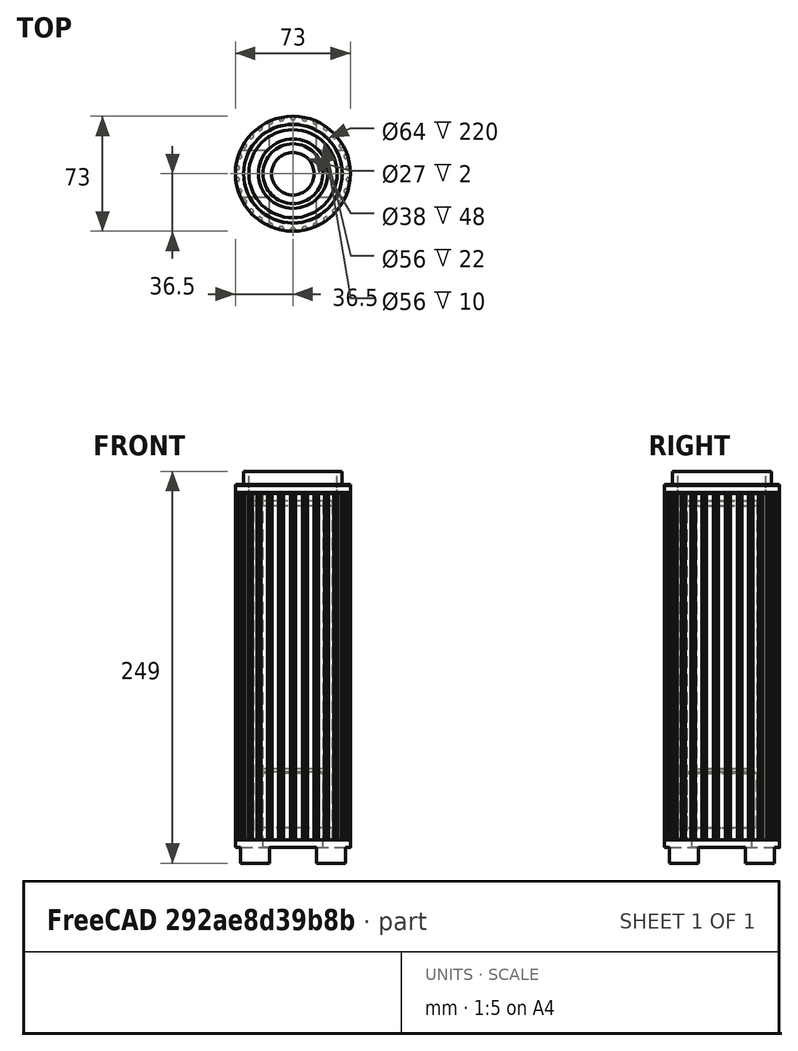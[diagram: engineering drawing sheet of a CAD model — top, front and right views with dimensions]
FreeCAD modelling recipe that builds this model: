
FCSTD DOCUMENT  (FreeCAD 0.15R4671 (Git))
Label: pica-small-v6
License: All rights reserved
LicenseURL: http://en.wikipedia.org/wiki/All_rights_reserved
objects: Drawing::FeatureView×16, Part::Cylinder×14, Part::Cut×7, Drawing::FeatureViewPart×7, Part::MultiFuse×6, Drawing::FeaturePage×2, Part::Box×2, Part::Part2DObjectPython×1, PartDesign::Pad×1, Part::Chamfer×1
note: 33 computed .brp shape members not serialized (recipe doc carries the construction recipe); baked Part::Feature solids carry a one-line shape summary decoded from their .brp

FEATURE [Part::Part2DObjectPython] InvoluteGear  # Draft 2D object (typed FeaturePython)
  ExternalGear = true
  HighPrecision = true
  Modules = 2.5
  NumberOfTeeth = 30
  PressureAngle = 20
FEATURE [PartDesign::Pad] Pad
  Length = 220
  Length2 = 100
  Sketch = -> InvoluteGear
  Type = 0
FEATURE [Part::Cylinder] Cylinder
  Angle = 360
  Height = 240
  Placement = pos=(0,0,-10) rot=(0,0,1;0rad)
  Radius = 32
FEATURE [Part::Cut] Cut  label="Final"
  Base = -> Pad
  Tool = -> Cylinder
FEATURE [Part::Cylinder] Cylinder001
  Angle = 360
  Height = 400
  Radius = 36.5
FEATURE [Part::Cylinder] Cylinder002
  Angle = 360
  Height = 400
  Radius = 100
FEATURE [Part::Cut] Cut001
  Base = -> Cylinder002
  Tool = -> Cylinder001
FEATURE [Part::Cut] Cut002  label="Shade"
  Base = -> Cut
  Placement = pos=(0,0,15) rot=(0,0,1;0rad)
  Tool = -> Cut001
FEATURE [Part::Cylinder] Cylinder003
  Angle = 360
  Height = 15
  Radius = 36.5
FEATURE [Part::Cylinder] Cylinder004
  Angle = 360
  Height = 22.5
  Radius = 31.3
FEATURE [Part::MultiFuse] Fusion  label="Base Fusion"
  Shapes = -> [Cylinder004,Cylinder003]
FEATURE [Drawing::FeatureViewPart] FrontView  label="Shade Side"
  Direction = (0,-1,0)
  HiddenWidth = 0.15
  LineWidth = 0.35
  Rotation = 90
  ShowHiddenLines = true
  ShowSmoothLines = false
  Source = -> Cut002
  Tolerance = 0.05
  ViewResult = <blob: 104580 chars omitted>
  Visible = true
  X = 80
  Y = 270
FEATURE [Drawing::FeatureViewPart] View001  label="Shade Top"
  Direction = (0,0,1)
  HiddenWidth = 0.15
  LineWidth = 0.35
  Rotation = 0
  ShowHiddenLines = false
  ShowSmoothLines = false
  Source = -> Cut002
  Tolerance = 0.05
  ViewResult = <blob: 17331 chars omitted>
  Visible = true
  X = 300
  Y = 80
FEATURE [Drawing::FeatureView] dim006  label="Base Radius"
  Rotation = 0
  ViewResult = <g   >\n <circle cx ="300.000000" cy ="170.000000" r="0.500000" stroke="none" fill="rgb(0,0,0)" /> \n<line x1="255.718312" y1="135.631286" x2="300.000000" y2="170.000000" style="stroke:rgb(0,0,0);stroke-width:0.30" />\n<polygon points="275.273643,150.808927 277.030448,153.438307 278.433561,153.261461 278.256715,151.858348" style="fill:rgb(0,0,0);stroke:rgb(0,0,0);stroke-width:0" />\n<line x1="255.718312" y1="135.631286" x2="231.639949" y2="135.631286" style="stroke:rgb(0,0,0);stroke-width:0.30" />\n<text x="219.448373" y="136.850443" font-family="Arial" font-size="3.6" fill="rgb(0,0,0)" text-anchor="inherit"  >R31.3</text>\n<!--31.3-->\n<!--R%3.3f-->\n</g> 
  Visible = true
  X = 0
  Y = 0
FEATURE [Drawing::FeatureView] centerLines
  Rotation = 0
  ViewResult = <g  transform="scale(1.000000,1.000000)" stroke="rgb(0,0,0)"  stroke-width="0.300000" >\n<path d="M 300.000000,170.000000 L 300.000000,168.000000 M 300.000000,166.000000 L 300.000000,160.000000 M 300.000000,158.000000 L 300.000000,156.000000 "/>\n<path d="M 300.000000,170.000000 L 302.000000,170.000000 M 304.000000,170.000000 L 310.000000,170.000000 M 312.000000,170.000000 L 314.000000,170.000000 "/>\n<path d="M 300.000000,170.000000 L 300.000000,172.000000 M 300.000000,174.000000 L 300.000000,180.000000 M 300.000000,182.000000 L 300.000000,184.000000 "/>\n<path d="M 300.000000,170.000000 L 298.000000,170.000000 M 296.000000,170.000000 L 290.000000,170.000000 M 288.000000,170.000000 L 286.000000,170.000000 "/>\n</g> 
  Visible = true
  X = 0
  Y = 0
FEATURE [Drawing::FeatureView] centerLines001
  Rotation = 0
  ViewResult = <g  transform="scale(1.000000,1.000000)" stroke="rgb(0,0,0)"  stroke-width="0.300000" >\n<path d="M 300.000000,80.000000 L 300.000000,82.000000 M 300.000000,84.000000 L 300.000000,90.000000 M 300.000000,92.000000 L 300.000000,94.000000 "/>\n<path d="M 300.000000,80.000000 L 302.000000,80.000000 M 304.000000,80.000000 L 310.000000,80.000000 M 312.000000,80.000000 L 314.000000,80.000000 "/>\n<path d="M 300.000000,80.000000 L 300.000000,78.000000 M 300.000000,76.000000 L 300.000000,70.000000 M 300.000000,68.000000 L 300.000000,66.000000 "/>\n<path d="M 300.000000,80.000000 L 298.000000,80.000000 M 296.000000,80.000000 L 290.000000,80.000000 M 288.000000,80.000000 L 286.000000,80.000000 "/>\n</g> 
  Visible = true
  X = 0
  Y = 0
FEATURE [Drawing::FeatureView] dim007  label="Shade Radius"
  Rotation = 0
  ViewResult = <g   >\n <circle cx ="300.000000" cy ="80.000000" r="0.500000" stroke="none" fill="rgb(0,0,0)" /> \n<line x1="340.917441" y1="111.884102" x2="300.000000" y2="80.000000" style="stroke:rgb(0,0,0);stroke-width:0.30" />\n<polygon points="325.241495,99.668933 323.489759,97.036174 322.086308,97.210316 322.260451,98.613767" style="fill:rgb(0,0,0);stroke:rgb(0,0,0);stroke-width:0" />\n<line x1="340.917441" y1="111.884102" x2="365.557939" y2="111.884102" style="stroke:rgb(0,0,0);stroke-width:0.30" />\n<text x="369.473360" y="112.835313" font-family="Arial" font-size="3.6" fill="rgb(0,0,0)" text-anchor="inherit"  >R32</text>\n<!--32.0-->\n<!--R%3.3f-->\n</g> 
  Visible = true
  X = 0
  Y = 0
FEATURE [Part::Cylinder] Cylinder005
  Angle = 360
  Height = 90
  Radius = 13.5
FEATURE [Part::Cylinder] Cylinder006
  Angle = 360
  Height = 58
  Radius = 19
FEATURE [Part::MultiFuse] Fusion002  label="Fixture Mount"
  Shapes = -> [Cylinder005,Cylinder006]
FEATURE [Drawing::FeatureViewPart] View004  label="Base Top"
  Direction = (0,0,1)
  HiddenWidth = 0.15
  LineWidth = 0.35
  Rotation = 0
  ShowHiddenLines = false
  ShowSmoothLines = false
  Tolerance = 0.05
  ViewResult = <g id="Base Top"\n   transform="rotate(0,300,170) translate(300,170) scale(1,1)"\n  >\n<g   stroke="rgb(0, 0, 0)"\n   stroke-width="0.35"\n   stroke-linecap="butt"\n   stroke-linejoin="miter"\n   fill="none"\n   transform="scale(1,-1)"\n  >\n<circle cx ="0" cy ="0" r ="23.3" /><circle cx ="0" cy ="0" r ="15" /><circle cx ="0" cy ="0" r ="31.3" /><circle cx ="0" cy ="0" r ="36.5" /></g>\n</g>
  Visible = true
  X = 300
  Y = 170
FEATURE [Drawing::FeatureViewPart] View005  label="Base Side"
  Direction = (0,-1,0)
  HiddenWidth = 0.15
  LineWidth = 0.35
  Rotation = 90
  ShowHiddenLines = false
  ShowSmoothLines = false
  Tolerance = 0.05
  ViewResult = <blob: 2600 chars omitted>
  Visible = true
  X = 80
  Y = 270
FEATURE [Drawing::FeatureViewPart] View  label="Base Side001"
  Direction = (0,-1,0)
  HiddenWidth = 0.15
  LineWidth = 0.35
  Rotation = 90
  ShowHiddenLines = false
  ShowSmoothLines = false
  Tolerance = 0.05
  ViewResult = <blob: 2605 chars omitted>
  Visible = true
  X = 180
  Y = 100
FEATURE [Drawing::FeatureViewPart] View006  label="Base Top001"
  Direction = (0,0,-1)
  HiddenWidth = 0.15
  LineWidth = 0.35
  Rotation = 0
  ShowHiddenLines = false
  ShowSmoothLines = false
  Tolerance = 0.05
  ViewResult = <blob: 2659 chars omitted>
  Visible = true
  X = 180
  Y = 170
FEATURE [Drawing::FeatureView] dim010  label="dim001"
  Rotation = 0
  ViewResult = <g   >\n<line x1="158.500000" y1="235.000000" x2="177.679727" y2="235.000000" style="stroke:rgb(0,0,0);stroke-width:0.30" />\n<line x1="158.483300" y1="250.000000" x2="177.679727" y2="250.000000" style="stroke:rgb(0,0,0);stroke-width:0.30" />\n<line x1="176.679727" y1="235.000000" x2="176.679727" y2="250.000000" style="stroke:rgb(0,0,0);stroke-width:0.30" />\n<polygon points="176.679727,235.000000 175.679727,238.000000 176.679727,239.000000 177.679727,238.000000" style="fill:rgb(0,0,0);stroke:rgb(0,0,0);stroke-width:0" /><polygon points="176.679727,250.000000 177.679727,247.000000 176.679727,246.000000 175.679727,247.000000" style="fill:rgb(0,0,0);stroke:rgb(0,0,0);stroke-width:0" />\n<text x="183.587709" y="244.783611" font-family="Arial" font-size="3.6" fill="rgb(0,0,0)" text-anchor="inherit" transform="rotate(-90.000000 183.587709,244.783611)" >15</text>\n</g> 
  Visible = true
  X = 0
  Y = 0
FEATURE [Drawing::FeatureView] dim011  label="dim002"
  Rotation = 0
  ViewResult = <g   >\n<line x1="153.300000" y1="228.000000" x2="177.810311" y2="228.000000" style="stroke:rgb(0,0,0);stroke-width:0.30" />\n<line x1="158.500000" y1="235.000000" x2="177.810311" y2="235.000000" style="stroke:rgb(0,0,0);stroke-width:0.30" />\n<line x1="176.810311" y1="228.000000" x2="176.810311" y2="235.000000" style="stroke:rgb(0,0,0);stroke-width:0.30" />\n<polygon points="176.810311,228.000000 177.810311,225.000000 176.810311,224.000000 175.810311,225.000000" style="fill:rgb(0,0,0);stroke:rgb(0,0,0);stroke-width:0" /><polygon points="176.810311,235.000000 175.810311,238.000000 176.810311,239.000000 177.810311,238.000000" style="fill:rgb(0,0,0);stroke:rgb(0,0,0);stroke-width:0" />\n<text x="183.208911" y="232.569545" font-family="Arial" font-size="3.6" fill="rgb(0,0,0)" text-anchor="inherit" transform="rotate(-90.000000 183.208911,232.569545)" >7</text>\n</g> 
  Visible = true
  X = 0
  Y = 0
FEATURE [Drawing::FeatureView] centerLines004
  Rotation = 0
  ViewResult = <g  transform="scale(1.000000,1.000000)" stroke="rgb(0,0,0)"  stroke-width="0.300000" >\n<path d="M 180.000000,169.999925 L 180.000000,167.999925 M 180.000000,165.999925 L 180.000000,159.999925 M 180.000000,157.999925 L 180.000000,155.999925 "/>\n<path d="M 180.000000,169.999925 L 182.000000,169.999925 M 184.000000,169.999925 L 190.000000,169.999925 M 192.000000,169.999925 L 194.000000,169.999925 "/>\n<path d="M 180.000000,169.999925 L 180.000000,171.999925 M 180.000000,173.999925 L 180.000000,179.999925 M 180.000000,181.999925 L 180.000000,183.999925 M 180.000000,185.999925 L 180.000000,186.160469 "/>\n<path d="M 180.000000,169.999925 L 178.000000,169.999925 M 176.000000,169.999925 L 170.000000,169.999925 M 168.000000,169.999925 L 166.583365,169.999925 "/>\n</g> 
  Visible = true
  X = 0
  Y = 0
FEATURE [Drawing::FeatureView] dim
  Rotation = 0
  ViewResult = <g   >\n<line x1="41.500000" y1="25.000000" x2="33.944194" y2="25.000000" style="stroke:rgb(0,0,0);stroke-width:0.30" />\n<line x1="41.500000" y1="245.000000" x2="33.944194" y2="245.000000" style="stroke:rgb(0,0,0);stroke-width:0.30" />\n<line x1="34.944194" y1="25.000000" x2="34.944194" y2="245.000000" style="stroke:rgb(0,0,0);stroke-width:0.30" />\n<polygon points="34.944194,25.000000 33.944194,28.000000 34.944194,29.000000 35.944194,28.000000" style="fill:rgb(0,0,0);stroke:rgb(0,0,0);stroke-width:0" /><polygon points="34.944194,245.000000 35.944194,242.000000 34.944194,241.000000 33.944194,242.000000" style="fill:rgb(0,0,0);stroke:rgb(0,0,0);stroke-width:0" />\n<text x="31.608126" y="136.256650" font-family="Arial" font-size="3.6" fill="rgb(0,0,0)" text-anchor="inherit" transform="rotate(-90.000000 31.608126,136.256650)" >220</text>\n</g> 
  Visible = true
  X = 0
  Y = 0
FEATURE [Drawing::FeatureView] dim012
  Rotation = 0
  ViewResult = <g   >\n<line x1="118.122400" y1="245.000000" x2="126.861722" y2="245.000000" style="stroke:rgb(0,0,0);stroke-width:0.30" />\n<line x1="115.275400" y1="270.000000" x2="126.861722" y2="270.000000" style="stroke:rgb(0,0,0);stroke-width:0.30" />\n<line x1="125.861722" y1="245.000000" x2="125.861722" y2="270.000000" style="stroke:rgb(0,0,0);stroke-width:0.30" />\n<polygon points="125.861722,245.000000 124.861722,248.000000 125.861722,249.000000 126.861722,248.000000" style="fill:rgb(0,0,0);stroke:rgb(0,0,0);stroke-width:0" /><polygon points="125.861722,270.000000 126.861722,267.000000 125.861722,266.000000 124.861722,267.000000" style="fill:rgb(0,0,0);stroke:rgb(0,0,0);stroke-width:0" />\n<text x="132.056471" y="260.197520" font-family="Arial" font-size="3.6" fill="rgb(0,0,0)" text-anchor="inherit" transform="rotate(-90.000000 132.056471,260.197520)" >25</text>\n</g> 
  Visible = true
  X = 0
  Y = 0
FEATURE [Drawing::FeatureView] dim013
  Rotation = 0
  ViewResult = <g   >\n<line x1="143.500000" y1="73.000000" x2="143.500000" y2="45.465562" style="stroke:rgb(0,0,0);stroke-width:0.30" />\n<line x1="216.500000" y1="73.000000" x2="216.500000" y2="45.465562" style="stroke:rgb(0,0,0);stroke-width:0.30" />\n<line x1="143.500000" y1="46.465562" x2="216.500000" y2="46.465562" style="stroke:rgb(0,0,0);stroke-width:0.30" />\n<polygon points="143.500000,46.465562 146.500000,47.465562 147.500000,46.465562 146.500000,45.465562" style="fill:rgb(0,0,0);stroke:rgb(0,0,0);stroke-width:0" /><polygon points="216.500000,46.465562 213.500000,45.465562 212.500000,46.465562 213.500000,47.465562" style="fill:rgb(0,0,0);stroke:rgb(0,0,0);stroke-width:0" />\n<text x="177.413963" y="43.541156" font-family="Arial" font-size="3.6" fill="rgb(0,0,0)" text-anchor="inherit" transform="rotate(0.000000 177.413963,43.541156)" >73</text>\n</g> 
  Visible = true
  X = 0
  Y = 0
FEATURE [Drawing::FeaturePage] AutoDrawing  label="Initial Sketch"
  EditableTexts = FLOYD DIEBEL | 8/22/2015 | 1:1 | 1 | 1 | PICA (SMALL V2) | LAMP WITH SHADE
  Group = -> [FrontView,View001,dim006,centerLines,centerLines001,dim007,View004,View005,dim010,dim011,View,View006,centerLines004,dim,dim012,dim013]
  Template = C:/Program Files/FreeCAD 0.15/data/Mod/Drawing/Templates/A3_Landscape.svg
FEATURE [Part::Cylinder] Cylinder007
  Angle = 360
  Height = 60
  Radius = 22
FEATURE [Part::MultiFuse] Fusion003
  Shapes = -> [Fusion,Cylinder007]
FEATURE [Part::Cut] Cut005  label="Raw"
  Base = -> Fusion003
  Tool = -> Fusion002
FEATURE [Part::Box] Box002  label="Cube002"
  Height = 10
  Length = 100
  Placement = pos=(-50,-15,0) rot=(0,0,1;0rad)
  Width = 30
FEATURE [Part::Box] Box003  label="Cube003"
  Height = 10
  Length = 100
  Placement = pos=(15,-50,0) rot=(0,0,1;1.5708rad)
  Width = 30
FEATURE [Part::MultiFuse] Fusion004  label="Feet Cutout Fusion001"
  Shapes = -> [Box003,Box002]
FEATURE [Part::Cut] Cut006  label="Pre-chamfer"
  Base = -> Cut005
  Tool = -> Fusion004
FEATURE [Part::Chamfer] Chamfer  label="Base"
  Base = -> Cut006
  Edges = 1 edges r=3: [Edge1]
FEATURE [Part::Cylinder] Cylinder008
  Angle = 360
  Height = 5
  Placement = pos=(0,0,8.5) rot=(0,0,1;0rad)
  Radius = 36.5
FEATURE [Part::Cylinder] Cylinder009
  Angle = 360
  Height = 22
  Radius = 31.3
FEATURE [Part::MultiFuse] Fusion005  label="No Cutout"
  Shapes = -> [Cylinder009,Cylinder008]
FEATURE [Part::Cylinder] Cylinder010
  Angle = 360
  Height = 55
  Placement = pos=(0,0,-10) rot=(0,0,1;0rad)
  Radius = 28
FEATURE [Part::Cut] Cut007  label="Joint"
  Base = -> Fusion005
  Placement = pos=(0,0,227) rot=(0,0,1;0rad)
  Tool = -> Cylinder010
FEATURE [Part::Cylinder] Cylinder011
  Angle = 360
  Height = 5
  Placement = pos=(0,0,5) rot=(0,0,1;0rad)
  Radius = 36.5
FEATURE [Part::Cylinder] Cylinder012
  Angle = 360
  Height = 10
  Radius = 31.3
FEATURE [Part::MultiFuse] Fusion006  label="No Cutout001"
  Shapes = -> [Cylinder012,Cylinder011]
FEATURE [Part::Cylinder] Cylinder013
  Angle = 360
  Height = 55
  Placement = pos=(0,0,-10) rot=(0,0,1;0rad)
  Radius = 28
FEATURE [Part::Cut] Cut008  label="Cap"
  Base = -> Fusion006
  Placement = pos=(0,0,230) rot=(0,0,1;0rad)
  Tool = -> Cylinder013
FEATURE [Drawing::FeatureViewPart] View008
  Direction = (1,0,0)
  HiddenWidth = 0.15
  LineWidth = 0.35
  Rotation = 270
  ShowHiddenLines = true
  ShowSmoothLines = false
  Source = -> Chamfer
  Tolerance = 0.05
  ViewResult = <blob: 14622 chars omitted>
  Visible = true
  X = 110
  Y = 150
FEATURE [Drawing::FeatureView] dim001  label="dim014"
  Rotation = 0
  ViewResult = <g> \n  <line x1="89.119500" y1="92.000000" x2="60.460732" y2="92.000000" style="stroke:rgb(0,0,0);stroke-width:0.30" />\n<line x1="89.119500" y1="90.000000" x2="60.460732" y2="90.000000" style="stroke:rgb(0,0,0);stroke-width:0.30" />\n<line x1="61.460732" y1="92.000000" x2="61.460732" y2="90.000000" style="stroke:rgb(0,0,0);stroke-width:0.30" /> \n  <polygon points="61.460732,90.000000 62.460732,87.000000 61.460732,86.000000 60.460732,87.000000" style="fill:rgb(0,0,0);stroke:rgb(0,0,0);stroke-width:0" /><polygon points="61.460732,92.000000 60.460732,95.000000 61.460732,96.000000 62.460732,95.000000" style="fill:rgb(0,0,0);stroke:rgb(0,0,0);stroke-width:0" /> \n  <text x="59.460732" y="91.000000" font-family="arial" font-size="3.6" fill="rgb(0,0,0)" text-anchor="middle" transform="rotate(-90.000000 59.460732,91.000000)" >2</text> </g>
  Visible = true
  X = 0
  Y = 0
FEATURE [Drawing::FeatureView] dim002  label="dim015"
  Rotation = 0
  ViewResult = <g> \n  <line x1="130.880500" y1="90.000000" x2="191.992125" y2="90.000000" style="stroke:rgb(0,0,0);stroke-width:0.30" />\n<line x1="145.275400" y1="150.000000" x2="191.992125" y2="150.000000" style="stroke:rgb(0,0,0);stroke-width:0.30" />\n<line x1="190.992125" y1="90.000000" x2="190.992125" y2="150.000000" style="stroke:rgb(0,0,0);stroke-width:0.30" /> \n  <polygon points="190.992125,150.000000 191.992125,147.000000 190.992125,146.000000 189.992125,147.000000" style="fill:rgb(0,0,0);stroke:rgb(0,0,0);stroke-width:0" /><polygon points="190.992125,90.000000 189.992125,93.000000 190.992125,94.000000 191.992125,93.000000" style="fill:rgb(0,0,0);stroke:rgb(0,0,0);stroke-width:0" /> \n  <text x="188.992125" y="120.000000" font-family="arial" font-size="3.6" fill="rgb(0,0,0)" text-anchor="middle" transform="rotate(-90.000000 188.992125,120.000000)" >60</text> </g>
  Visible = true
  X = 0
  Y = 0
FEATURE [Drawing::FeatureView] dim003
  Rotation = 0
  ViewResult = <g> \n  <line x1="133.861700" y1="93.000000" x2="168.857378" y2="93.000000" style="stroke:rgb(0,0,0);stroke-width:0.30" />\n<line x1="143.103200" y1="127.500000" x2="168.857378" y2="127.500000" style="stroke:rgb(0,0,0);stroke-width:0.30" />\n<line x1="167.857378" y1="93.000000" x2="167.857378" y2="127.500000" style="stroke:rgb(0,0,0);stroke-width:0.30" /> \n  <polygon points="167.857378,127.500000 168.857378,124.500000 167.857378,123.500000 166.857378,124.500000" style="fill:rgb(0,0,0);stroke:rgb(0,0,0);stroke-width:0" /><polygon points="167.857378,93.000000 166.857378,96.000000 167.857378,97.000000 168.857378,96.000000" style="fill:rgb(0,0,0);stroke:rgb(0,0,0);stroke-width:0" /> \n  <text x="165.857378" y="110.250000" font-family="arial" font-size="3.6" fill="rgb(0,0,0)" text-anchor="middle" transform="rotate(-90.000000 165.857378,110.250000)" >34.5</text> </g>
  Visible = true
  X = 0
  Y = 0
FEATURE [Drawing::FeatureView] dim004
  Rotation = 0
  ViewResult = <g> \n  <line x1="76.896800" y1="127.500000" x2="41.581851" y2="127.500000" style="stroke:rgb(0,0,0);stroke-width:0.30" />\n<line x1="71.729500" y1="135.000000" x2="41.581851" y2="135.000000" style="stroke:rgb(0,0,0);stroke-width:0.30" />\n<line x1="42.581851" y1="127.500000" x2="42.581851" y2="135.000000" style="stroke:rgb(0,0,0);stroke-width:0.30" /> \n  <polygon points="42.581851,135.000000 41.581851,138.000000 42.581851,139.000000 43.581851,138.000000" style="fill:rgb(0,0,0);stroke:rgb(0,0,0);stroke-width:0" /><polygon points="42.581851,127.500000 43.581851,124.500000 42.581851,123.500000 41.581851,124.500000" style="fill:rgb(0,0,0);stroke:rgb(0,0,0);stroke-width:0" /> \n  <text x="40.581851" y="131.250000" font-family="arial" font-size="3.6" fill="rgb(0,0,0)" text-anchor="middle" transform="rotate(-90.000000 40.581851,131.250000)" >7.5</text> </g>
  Visible = true
  X = 0
  Y = 0
FEATURE [Drawing::FeatureView] dim005
  Rotation = 0
  ViewResult = <g> \n  <line x1="148.270500" y1="135.000000" x2="177.589440" y2="135.000000" style="stroke:rgb(0,0,0);stroke-width:0.30" />\n<line x1="148.083300" y1="140.000000" x2="177.589440" y2="140.000000" style="stroke:rgb(0,0,0);stroke-width:0.30" />\n<line x1="176.589440" y1="135.000000" x2="176.589440" y2="140.000000" style="stroke:rgb(0,0,0);stroke-width:0.30" /> \n  <polygon points="176.589440,140.000000 175.589440,143.000000 176.589440,144.000000 177.589440,143.000000" style="fill:rgb(0,0,0);stroke:rgb(0,0,0);stroke-width:0" /><polygon points="176.589440,135.000000 177.589440,132.000000 176.589440,131.000000 175.589440,132.000000" style="fill:rgb(0,0,0);stroke:rgb(0,0,0);stroke-width:0" /> \n  <text x="174.589440" y="137.500000" font-family="arial" font-size="3.6" fill="rgb(0,0,0)" text-anchor="middle" transform="rotate(-90.000000 174.589440,137.500000)" >5</text> </g>
  Visible = true
  X = 0
  Y = 0
FEATURE [Drawing::FeatureView] dim008
  Rotation = 0
  ViewResult = <g> \n  <line x1="71.500000" y1="140.000000" x2="52.436048" y2="140.000000" style="stroke:rgb(0,0,0);stroke-width:0.30" />\n<line x1="74.724600" y1="150.000000" x2="52.436048" y2="150.000000" style="stroke:rgb(0,0,0);stroke-width:0.30" />\n<line x1="53.436048" y1="140.000000" x2="53.436048" y2="150.000000" style="stroke:rgb(0,0,0);stroke-width:0.30" /> \n  <polygon points="53.436048,150.000000 52.436048,153.000000 53.436048,154.000000 54.436048,153.000000" style="fill:rgb(0,0,0);stroke:rgb(0,0,0);stroke-width:0" /><polygon points="53.436048,140.000000 54.436048,137.000000 53.436048,136.000000 52.436048,137.000000" style="fill:rgb(0,0,0);stroke:rgb(0,0,0);stroke-width:0" /> \n  <text x="51.436048" y="145.000000" font-family="arial" font-size="3.6" fill="rgb(0,0,0)" text-anchor="middle" transform="rotate(-90.000000 51.436048,145.000000)" >10</text> </g>
  Visible = true
  X = 0
  Y = 0
FEATURE [Drawing::FeaturePage] Page
  EditableTexts = FLOYD DIEBEL | PICA BASE | MODIFIED LIP FOR LIGHT FIXTURE | A4 | 3 / 3 | 1:1 | 2016/06/02 | 6
  Group = -> [View008,dim001,dim002,dim003,dim004,dim005,dim008]
  Template = D:/Program Files/FreeCAD 0.15/data/Mod/Drawing/Templates/A4_Portrait_ISO7200.svg
